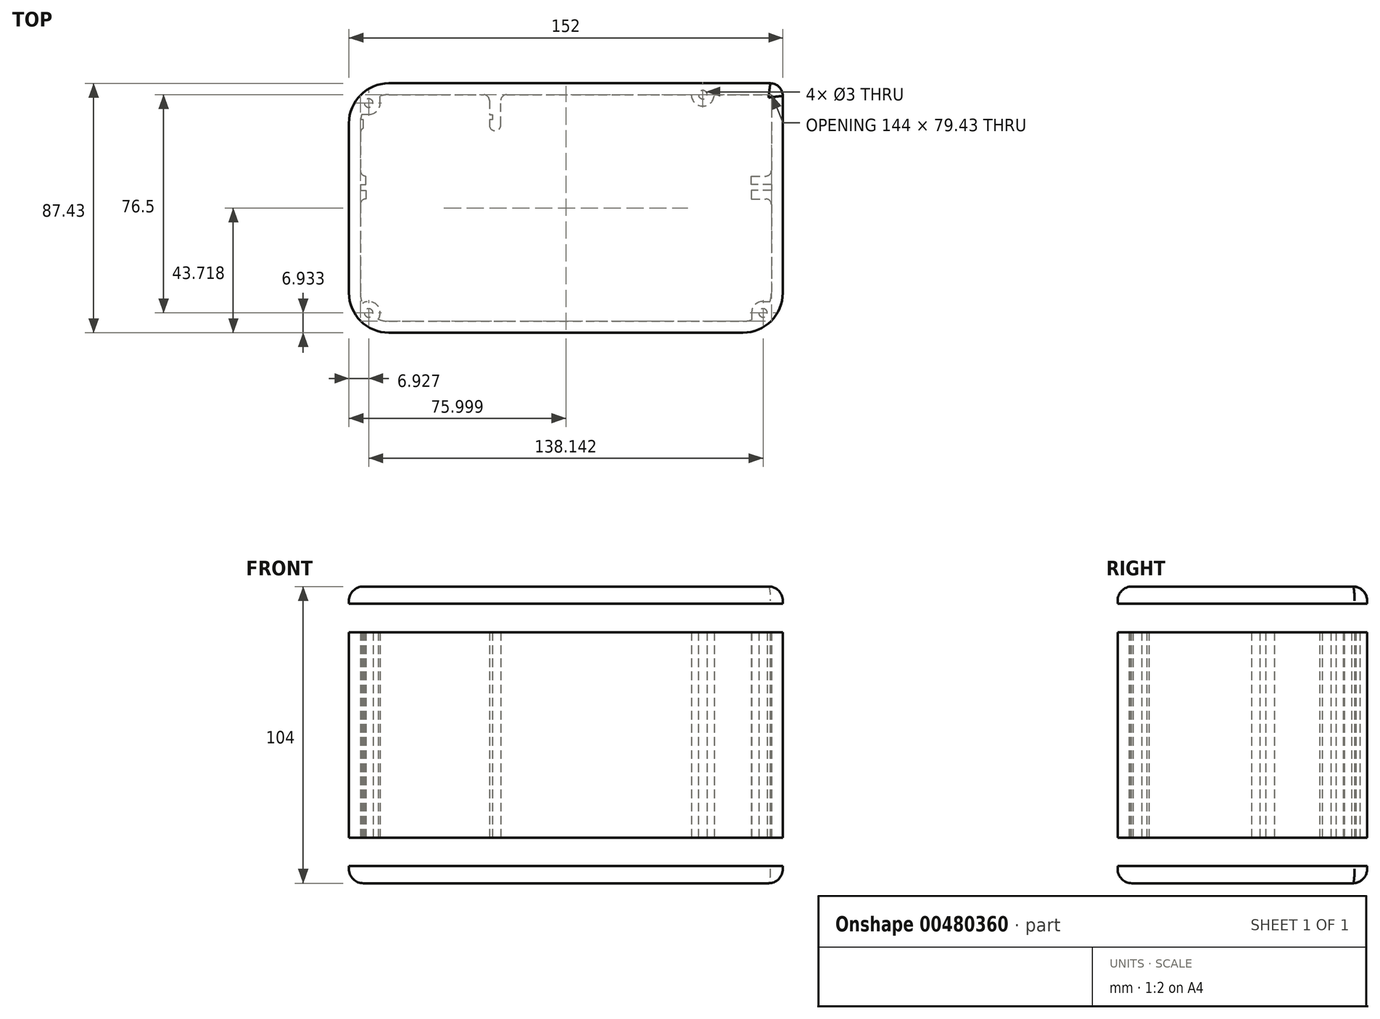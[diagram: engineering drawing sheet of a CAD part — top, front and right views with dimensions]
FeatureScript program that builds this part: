
annotation { "Feature Type Name" : "Feature", "Feature Type Description" : "" }
export const myFeature = defineFeature(function(context is Context, id is Id, definition is map)
    precondition{}
    {
        {
            var Q0;
            Q0=qCreatedBy(makeId("Top.planeOp"),FACE);
            var sketch = newSketch(context, id + "F0", { "sketchPlane" : qUnion([Q0])});
            skLineSegment(sketch, "E0.bottom", {"start": v(-110.78, -6.54) * mm, "end": v(28.22, -6.54) * mm, "construction": true});
            skLineSegment(sketch, "E0.top", {"start": v(-110.78, -8.34) * mm, "end": v(28.22, -8.34) * mm, "construction": true});
            skLineSegment(sketch, "E0.left", {"start": v(-110.78, -6.54) * mm, "end": v(-110.78, -8.34) * mm});
            skLineSegment(sketch, "E0.right", {"start": v(28.22, -6.54) * mm, "end": v(28.22, -8.34) * mm});
            skLineSegment(sketch, "E1.left", {"start": v(-107.28, -22.34) * mm, "end": v(-107.28, -42.34) * mm, "construction": true});
            skLineSegment(sketch, "E2.right", {"start": v(29.72, -22.34) * mm, "end": v(29.72, -42.34) * mm, "construction": true});
            skLineSegment(sketch, "E3.bottom", {"start": v(-100.78, 25.1) * mm, "end": v(32.82, 25.1) * mm});
            skLineSegment(sketch, "E3.top", {"start": v(-100.78, -54.34) * mm, "end": v(23.22, -54.34) * mm});
            skLineSegment(sketch, "E3.left", {"start": v(-110.78, 15.1) * mm, "end": v(-110.78, -44.34) * mm});
            skLineSegment(sketch, "E3.right", {"start": v(33.22, 24.7) * mm, "end": v(33.22, -44.34) * mm});
            skPoint(sketch, "E4", {"position": v(-38.78, -54.34) * mm});
            skPoint(sketch, "E5.visualSharp", {"position": v(-110.78, 25.1) * mm});
            skArc(sketch, "E5.filletArc", {"start": v(-100.78, 25.1) * mm, "mid": v(-107.85, 22.16) * mm, "end": v(-110.78, 15.1) * mm});
            skPoint(sketch, "E6.visualSharp", {"position": v(33.22, 25.1) * mm});
            skArc(sketch, "E6.filletArc", {"start": v(33.22, 24.7) * mm, "mid": v(33.1, 24.98) * mm, "end": v(32.82, 25.1) * mm});
            skPoint(sketch, "E7.visualSharp", {"position": v(33.22, -54.34) * mm});
            skArc(sketch, "E7.filletArc", {"start": v(23.22, -54.34) * mm, "mid": v(30.29, -51.4) * mm, "end": v(33.22, -44.34) * mm});
            skPoint(sketch, "E8.visualSharp", {"position": v(-110.78, -54.34) * mm});
            skArc(sketch, "E8.filletArc", {"start": v(-110.78, -44.34) * mm, "mid": v(-107.85, -51.4) * mm, "end": v(-100.78, -54.34) * mm});
            skLineSegment(sketch, "E9.0", {"start": v(-100.78, 29.1) * mm, "end": v(32.82, 29.1) * mm});
            skArc(sketch, "E9.1", {"start": v(37.22, 24.7) * mm, "mid": v(35.93, 27.8) * mm, "end": v(32.82, 29.1) * mm});
            skArc(sketch, "E9.2", {"start": v(-100.78, 29.1) * mm, "mid": v(-110.68, 25) * mm, "end": v(-114.78, 15.1) * mm});
            skLineSegment(sketch, "E9.3", {"start": v(37.22, 24.7) * mm, "end": v(37.22, -44.34) * mm});
            skLineSegment(sketch, "E9.4", {"start": v(-114.78, 15.1) * mm, "end": v(-114.78, -44.34) * mm});
            skArc(sketch, "E9.5", {"start": v(-114.78, -44.34) * mm, "mid": v(-110.68, -54.24) * mm, "end": v(-100.78, -58.34) * mm});
            skLineSegment(sketch, "E9.6", {"start": v(-100.78, -58.34) * mm, "end": v(23.22, -58.34) * mm});
            skArc(sketch, "E9.7", {"start": v(23.22, -58.34) * mm, "mid": v(33.12, -54.24) * mm, "end": v(37.22, -44.34) * mm});
            skLineSegment(sketch, "E10", {"start": v(-97.28, -12.34) * mm, "end": v(19.72, -12.34) * mm, "construction": true});
            skLineSegment(sketch, "E11", {"start": v(19.72, -52.34) * mm, "end": v(-97.28, -52.34) * mm, "construction": true});
            skLineSegment(sketch, "E12", {"start": v(-35.28, -12.34) * mm, "end": v(-35.28, -52.34) * mm, "construction": true});
            skPoint(sketch, "E13", {"position": v(-38.78, -12.34) * mm});
            skPoint(sketch, "E14.visualSharp", {"position": v(-107.28, -12.34) * mm});
            skArc(sketch, "E14.filletArc", {"start": v(-97.28, -12.34) * mm, "mid": v(-104.35, -15.27) * mm, "end": v(-107.28, -22.34) * mm, "construction": true});
            skPoint(sketch, "E15.visualSharp", {"position": v(-107.28, -52.34) * mm});
            skArc(sketch, "E15.filletArc", {"start": v(-107.28, -42.34) * mm, "mid": v(-104.35, -49.4) * mm, "end": v(-97.28, -52.34) * mm, "construction": true});
            skPoint(sketch, "E16.visualSharp", {"position": v(29.72, -52.34) * mm});
            skArc(sketch, "E16.filletArc", {"start": v(19.72, -52.34) * mm, "mid": v(26.79, -49.4) * mm, "end": v(29.72, -42.34) * mm, "construction": true});
            skPoint(sketch, "E17.visualSharp", {"position": v(29.72, -12.34) * mm});
            skArc(sketch, "E17.filletArc", {"start": v(29.72, -22.34) * mm, "mid": v(26.79, -15.27) * mm, "end": v(19.72, -12.34) * mm, "construction": true});
            skCircle(sketch, "E18", {"center": v(-107.85, 22.16) * mm, "radius": 4 * mm});
            skLineSegment(sketch, "E19", {"start": v(-100.78, 15.1) * mm, "end": v(-110.78, 25.1) * mm, "construction": true});
            skCircle(sketch, "E20", {"center": v(30.29, -51.4) * mm, "radius": 4 * mm});
            skLineSegment(sketch, "E21", {"start": v(23.22, -44.34) * mm, "end": v(33.22, -54.34) * mm, "construction": true});
            skCircle(sketch, "E22", {"center": v(-107.85, -51.4) * mm, "radius": 4 * mm});
            skLineSegment(sketch, "E23", {"start": v(-100.78, -44.34) * mm, "end": v(-110.78, -54.34) * mm, "construction": true});
            skLineSegment(sketch, "E24.bottom", {"start": v(-110.78, 18.06) * mm, "end": v(-64.58, 18.06) * mm});
            skLineSegment(sketch, "E24.top", {"start": v(-110.78, 16.46) * mm, "end": v(-64.58, 16.46) * mm});
            skLineSegment(sketch, "E24.left", {"start": v(-110.78, 18.06) * mm, "end": v(-110.78, 16.46) * mm});
            skLineSegment(sketch, "E24.right", {"start": v(-64.58, 18.06) * mm, "end": v(-64.58, 16.46) * mm});
            skLineSegment(sketch, "E25", {"start": v(-65.58, 25.1) * mm, "end": v(-65.58, 18.16) * mm});
            skLineSegment(sketch, "E26", {"start": v(-65.58, 18.16) * mm, "end": v(-64.58, 18.16) * mm});
            skLineSegment(sketch, "E27", {"start": v(-64.58, 18.16) * mm, "end": v(-64.58, 16.36) * mm});
            skLineSegment(sketch, "E28", {"start": v(-64.58, 16.36) * mm, "end": v(-65.58, 16.36) * mm});
            skLineSegment(sketch, "E29", {"start": v(-65.58, 16.36) * mm, "end": v(-65.58, 12.47) * mm});
            skLineSegment(sketch, "E30", {"start": v(-65.58, 12.47) * mm, "end": v(-61.58, 12.47) * mm});
            skLineSegment(sketch, "E31", {"start": v(-61.58, 12.47) * mm, "end": v(-61.58, 25.1) * mm});
            skPoint(sketch, "E32", {"position": v(-64.58, 17.26) * mm});
            skLineSegment(sketch, "E33", {"start": v(-110.78, 13.36) * mm, "end": v(-109.78, 13.36) * mm});
            skLineSegment(sketch, "E34", {"start": v(-109.78, 13.36) * mm, "end": v(-109.78, 16.36) * mm});
            skLineSegment(sketch, "E35", {"start": v(-109.78, 16.36) * mm, "end": v(-110.78, 16.36) * mm});
            skLineSegment(sketch, "E36", {"start": v(-107.85, 18.16) * mm, "end": v(-110.3, 18.16) * mm});
            skLineSegment(sketch, "E37", {"start": v(-103.85, 22.16) * mm, "end": v(-103.85, 24.6) * mm});
            skLineSegment(sketch, "E38", {"start": v(-107.85, -47.4) * mm, "end": v(-110.3, -47.4) * mm});
            skLineSegment(sketch, "E39", {"start": v(-103.85, -51.4) * mm, "end": v(-103.85, -53.85) * mm});
            skLineSegment(sketch, "E40", {"start": v(30.29, -47.4) * mm, "end": v(32.74, -47.4) * mm});
            skLineSegment(sketch, "E41", {"start": v(26.29, -51.4) * mm, "end": v(26.29, -53.85) * mm});
            skLineSegment(sketch, "E42", {"start": v(-110.78, -6.44) * mm, "end": v(-108.78, -6.44) * mm});
            skLineSegment(sketch, "E43", {"start": v(-108.78, -6.44) * mm, "end": v(-108.78, -3.44) * mm});
            skLineSegment(sketch, "E44", {"start": v(-108.78, -3.44) * mm, "end": v(-110.78, -3.44) * mm});
            skLineSegment(sketch, "E45", {"start": v(-110.78, -8.44) * mm, "end": v(-108.78, -8.44) * mm});
            skLineSegment(sketch, "E46", {"start": v(-108.78, -8.44) * mm, "end": v(-108.78, -11.44) * mm});
            skLineSegment(sketch, "E47", {"start": v(-108.78, -11.44) * mm, "end": v(-110.78, -11.44) * mm});
            skLineSegment(sketch, "E48", {"start": v(33.22, -6.44) * mm, "end": v(26.22, -6.44) * mm});
            skLineSegment(sketch, "E49", {"start": v(26.22, -6.44) * mm, "end": v(26.22, -3.44) * mm});
            skLineSegment(sketch, "E50", {"start": v(33.22, -8.44) * mm, "end": v(26.22, -8.44) * mm});
            skLineSegment(sketch, "E51", {"start": v(26.22, -8.44) * mm, "end": v(26.22, -11.44) * mm});
            skLineSegment(sketch, "E52", {"start": v(26.22, -11.44) * mm, "end": v(33.22, -11.44) * mm});
            skLineSegment(sketch, "E53", {"start": v(26.22, -3.44) * mm, "end": v(33.22, -3.44) * mm});
            skLineSegment(sketch, "E54", {"start": v(28.22, -6.44) * mm, "end": v(28.22, -8.44) * mm});
            skCircle(sketch, "E55", {"center": v(9.18, 25.1) * mm, "radius": 4 * mm});
            skCircle(sketch, "E56", {"center": v(9.18, 25.1) * mm, "radius": 1.5 * mm});
            skCircle(sketch, "E57", {"center": v(-107.85, 22.16) * mm, "radius": 1.5 * mm});
            skCircle(sketch, "E58", {"center": v(-107.85, -51.4) * mm, "radius": 1.5 * mm});
            skCircle(sketch, "E59", {"center": v(30.29, -51.4) * mm, "radius": 1.5 * mm});
            skSolve(sketch);
        }
        {
            var Q0;
            Q0=makeQuery(id+"F0.imprint","IMPRINT",FACE,{"disambiguationData":[TD([[makeQuery(id+"F0.imprint","IMPRINT",EDGE,{"derivedFrom":sQuery(id+"F0.wireOp",EDGE,"E3.bottom")}),1.0]])]});
            var Q1;
            {var subQ0=sQuery(id+"F0.wireOp",EDGE,"E18");var subQ1=sQuery(id+"F0.wireOp",EDGE,"E5.filletArc");var subQ2=makeQuery(id+"F0.imprint","INTERSECT",VERTEX,{"disambiguationData":[OD(0.0)],"derivedFrom":[subQ1,subQ0]});Q1=makeQuery(id+"F0.imprint","IMPRINT",FACE,{"disambiguationData":[TD([[makeQuery(id+"F0.imprint","IMPRINT",EDGE,{"disambiguationData":[TD([[subQ2,-1.0]])],"derivedFrom":subQ1}),-1.0]])]});}
            var Q2;
            {var subQ3=sQuery(id+"F0.wireOp",EDGE,"E25");Q2=makeQuery(id+"F0.imprint","IMPRINT",FACE,{"disambiguationData":[TD([[makeQuery(id+"F0.imprint","IMPRINT",EDGE,{"derivedFrom":subQ3}),1.0]])]});}
            var Q3;
            {var subQ1=sQuery(id+"F0.wireOp",EDGE,"E33");Q3=makeQuery(id+"F0.imprint","IMPRINT",FACE,{"disambiguationData":[TD([[makeQuery(id+"F0.imprint","IMPRINT",EDGE,{"derivedFrom":subQ1}),1.0]])]});}
            var Q4;
            {var subQ0=sQuery(id+"F0.wireOp",EDGE,"E37");Q4=makeQuery(id+"F0.imprint","IMPRINT",FACE,{"disambiguationData":[TD([[makeQuery(id+"F0.imprint","IMPRINT",EDGE,{"derivedFrom":subQ0}),1.0]])]});}
            var Q5;
            {var subQ0=sQuery(id+"F0.wireOp",EDGE,"E18");var subQ1=sQuery(id+"F0.wireOp",EDGE,"E5.filletArc");var subQ2=makeQuery(id+"F0.imprint","INTERSECT",VERTEX,{"disambiguationData":[OD(0.0)],"derivedFrom":[subQ1,subQ0]});Q5=makeQuery(id+"F0.imprint","IMPRINT",FACE,{"disambiguationData":[TD([[makeQuery(id+"F0.imprint","IMPRINT",EDGE,{"disambiguationData":[TD([[subQ2,-1.0]])],"derivedFrom":subQ1}),1.0]])]});}
            var Q6;
            {var subQ0=sQuery(id+"F0.wireOp",EDGE,"E36");Q6=makeQuery(id+"F0.imprint","IMPRINT",FACE,{"disambiguationData":[TD([[makeQuery(id+"F0.imprint","IMPRINT",EDGE,{"derivedFrom":subQ0}),-1.0]])]});}
            var Q7;
            {var subQ0=sQuery(id+"F0.wireOp",EDGE,"98a416b9-4927-4f26-95ba-e2e42b6dbb6d");var subQ1=sQuery(id+"F0.wireOp",EDGE,"E6.filletArc");var subQ2=makeQuery(id+"F0.imprint","INTERSECT",VERTEX,{"disambiguationData":[OD(0.0)],"derivedFrom":[subQ1,subQ0]});Q7=makeQuery(id+"F0.imprint","IMPRINT",FACE,{"disambiguationData":[TD([[makeQuery(id+"F0.imprint","IMPRINT",EDGE,{"disambiguationData":[TD([[subQ2,-1.0]])],"derivedFrom":subQ1}),-1.0]])]});}
            var Q8;
            {var subQ0=sQuery(id+"F0.wireOp",EDGE,"7a0X1hN1-dMAj-nVcP-FXcl-xYdpotMuzt6M");Q8=makeQuery(id+"F0.imprint","IMPRINT",FACE,{"disambiguationData":[TD([[makeQuery(id+"F0.imprint","IMPRINT",EDGE,{"derivedFrom":subQ0}),-1.0]])]});}
            var Q9;
            {var subQ0=sQuery(id+"F0.wireOp",EDGE,"7hl1VtTn-0XGv-oFa7-S9O5-PqMMbb4nXPVR");Q9=makeQuery(id+"F0.imprint","IMPRINT",FACE,{"disambiguationData":[TD([[makeQuery(id+"F0.imprint","IMPRINT",EDGE,{"derivedFrom":subQ0}),1.0]])]});}
            var Q10;
            {var subQ1=sQuery(id+"F0.wireOp",EDGE,"E9.3");Q10=makeQuery(id+"F0.imprint","IMPRINT",FACE,{"disambiguationData":[TD([[makeQuery(id+"F0.imprint","IMPRINT",EDGE,{"derivedFrom":subQ1}),-1.0]])]});}
            var Q11;
            {var subQ0=sQuery(id+"F0.wireOp",EDGE,"E20");var subQ1=sQuery(id+"F0.wireOp",EDGE,"E7.filletArc");var subQ2=makeQuery(id+"F0.imprint","INTERSECT",VERTEX,{"disambiguationData":[OD(0.0)],"derivedFrom":[subQ1,subQ0]});Q11=makeQuery(id+"F0.imprint","IMPRINT",FACE,{"disambiguationData":[TD([[makeQuery(id+"F0.imprint","IMPRINT",EDGE,{"disambiguationData":[TD([[subQ2,-1.0]])],"derivedFrom":subQ1}),-1.0]])]});}
            var Q12;
            {var subQ0=sQuery(id+"F0.wireOp",EDGE,"E20");var subQ1=sQuery(id+"F0.wireOp",EDGE,"E7.filletArc");var subQ2=makeQuery(id+"F0.imprint","INTERSECT",VERTEX,{"disambiguationData":[OD(0.0)],"derivedFrom":[subQ1,subQ0]});Q12=makeQuery(id+"F0.imprint","IMPRINT",FACE,{"disambiguationData":[TD([[makeQuery(id+"F0.imprint","IMPRINT",EDGE,{"disambiguationData":[TD([[subQ2,-1.0]])],"derivedFrom":subQ1}),1.0]])]});}
            var Q13;
            {var subQ0=sQuery(id+"F0.wireOp",EDGE,"E40");var subQ1=sQuery(id+"F0.wireOp",EDGE,"E7.filletArc");var subQ2=makeQuery(id+"F0.imprint","INTERSECT",VERTEX,{"derivedFrom":[subQ1,subQ0]});Q13=makeQuery(id+"F0.imprint","IMPRINT",FACE,{"disambiguationData":[TD([[makeQuery(id+"F0.imprint","IMPRINT",EDGE,{"disambiguationData":[TD([[subQ2,1.0]])],"derivedFrom":subQ1}),1.0]])]});}
            var Q14;
            {var subQ0=sQuery(id+"F0.wireOp",EDGE,"E20");var subQ1=sQuery(id+"F0.wireOp",EDGE,"E16.filletArc");var subQ2=makeQuery(id+"F0.imprint","INTERSECT",VERTEX,{"disambiguationData":[OD(0.0)],"derivedFrom":[subQ1,subQ0]});Q14=makeQuery(id+"F0.imprint","IMPRINT",FACE,{"disambiguationData":[TD([[makeQuery(id+"F0.imprint","IMPRINT",EDGE,{"disambiguationData":[TD([[subQ2,-1.0]])],"derivedFrom":subQ1}),1.0]])]});}
            var Q15;
            {var subQ0=sQuery(id+"F0.wireOp",EDGE,"E41");var subQ1=sQuery(id+"F0.wireOp",EDGE,"E7.filletArc");var subQ2=makeQuery(id+"F0.imprint","INTERSECT",VERTEX,{"derivedFrom":[subQ1,subQ0]});Q15=makeQuery(id+"F0.imprint","IMPRINT",FACE,{"disambiguationData":[TD([[makeQuery(id+"F0.imprint","IMPRINT",EDGE,{"disambiguationData":[TD([[subQ2,-1.0]])],"derivedFrom":subQ1}),1.0]])]});}
            var Q16;
            {var subQ9=sQuery(id+"F0.wireOp",EDGE,"E3.top");Q16=makeQuery(id+"F0.imprint","IMPRINT",FACE,{"disambiguationData":[TD([[makeQuery(id+"F0.imprint","IMPRINT",EDGE,{"derivedFrom":subQ9}),-1.0]])]});}
            var Q17;
            {var subQ0=sQuery(id+"F0.wireOp",EDGE,"E22");var subQ1=sQuery(id+"F0.wireOp",EDGE,"E8.filletArc");var subQ2=makeQuery(id+"F0.imprint","INTERSECT",VERTEX,{"disambiguationData":[OD(0.0)],"derivedFrom":[subQ1,subQ0]});Q17=makeQuery(id+"F0.imprint","IMPRINT",FACE,{"disambiguationData":[TD([[makeQuery(id+"F0.imprint","IMPRINT",EDGE,{"disambiguationData":[TD([[subQ2,-1.0]])],"derivedFrom":subQ1}),-1.0]])]});}
            var Q18;
            {var subQ0=sQuery(id+"F0.wireOp",EDGE,"E22");var subQ1=sQuery(id+"F0.wireOp",EDGE,"E8.filletArc");var subQ2=makeQuery(id+"F0.imprint","INTERSECT",VERTEX,{"disambiguationData":[OD(0.0)],"derivedFrom":[subQ1,subQ0]});Q18=makeQuery(id+"F0.imprint","IMPRINT",FACE,{"disambiguationData":[TD([[makeQuery(id+"F0.imprint","IMPRINT",EDGE,{"disambiguationData":[TD([[subQ2,-1.0]])],"derivedFrom":subQ1}),1.0]])]});}
            var Q19;
            {var subQ0=sQuery(id+"F0.wireOp",EDGE,"E22");var subQ1=sQuery(id+"F0.wireOp",EDGE,"E15.filletArc");var subQ2=makeQuery(id+"F0.imprint","INTERSECT",VERTEX,{"disambiguationData":[OD(0.0)],"derivedFrom":[subQ1,subQ0]});Q19=makeQuery(id+"F0.imprint","IMPRINT",FACE,{"disambiguationData":[TD([[makeQuery(id+"F0.imprint","IMPRINT",EDGE,{"disambiguationData":[TD([[subQ2,-1.0]])],"derivedFrom":subQ1}),1.0]])]});}
            var Q20;
            {var subQ0=sQuery(id+"F0.wireOp",EDGE,"E48");Q20=makeQuery(id+"F0.imprint","IMPRINT",FACE,{"disambiguationData":[TD([[makeQuery(id+"F0.imprint","IMPRINT",EDGE,{"derivedFrom":subQ0}),-1.0]])]});}
            var Q21;
            {var subQ0=sQuery(id+"F0.wireOp",EDGE,"E50");Q21=makeQuery(id+"F0.imprint","IMPRINT",FACE,{"disambiguationData":[TD([[makeQuery(id+"F0.imprint","IMPRINT",EDGE,{"derivedFrom":subQ0}),1.0]])]});}
            var Q22;
            {var subQ0=sQuery(id+"F0.wireOp",EDGE,"E42");Q22=makeQuery(id+"F0.imprint","IMPRINT",FACE,{"disambiguationData":[TD([[makeQuery(id+"F0.imprint","IMPRINT",EDGE,{"derivedFrom":subQ0}),1.0]])]});}
            var Q23;
            {var subQ0=sQuery(id+"F0.wireOp",EDGE,"E45");Q23=makeQuery(id+"F0.imprint","IMPRINT",FACE,{"disambiguationData":[TD([[makeQuery(id+"F0.imprint","IMPRINT",EDGE,{"derivedFrom":subQ0}),-1.0]])]});}
            var Q24;
            {var subQ0=sQuery(id+"F0.wireOp",EDGE,"E54");var subQ3=makeQuery(id+"F0.imprint","IMPRINT",VERTEX,{"disambiguationData":[OD(0.0)],"derivedFrom":subQ0});Q24=makeQuery(id+"F0.imprint","IMPRINT",FACE,{"disambiguationData":[TD([[makeQuery(id+"F0.imprint","IMPRINT",EDGE,{"disambiguationData":[TD([[subQ3,-1.0]])],"derivedFrom":subQ0}),1.0]])]});}
            var Q25;
            {var subQ0=sQuery(id+"F0.wireOp",EDGE,"E55");var subQ1=sQuery(id+"F0.wireOp",EDGE,"E3.bottom");var subQ2=makeQuery(id+"F0.imprint","INTERSECT",VERTEX,{"disambiguationData":[OD(0.0)],"derivedFrom":[subQ1,subQ0]});Q25=makeQuery(id+"F0.imprint","IMPRINT",FACE,{"disambiguationData":[TD([[makeQuery(id+"F0.imprint","IMPRINT",EDGE,{"disambiguationData":[TD([[subQ2,-1.0]])],"derivedFrom":subQ1}),1.0]])]});}
            var Q26;
            {var subQ0=sQuery(id+"F0.wireOp",EDGE,"E55");var subQ1=sQuery(id+"F0.wireOp",EDGE,"E3.bottom");var subQ2=makeQuery(id+"F0.imprint","INTERSECT",VERTEX,{"disambiguationData":[OD(0.0)],"derivedFrom":[subQ1,subQ0]});Q26=makeQuery(id+"F0.imprint","IMPRINT",FACE,{"disambiguationData":[TD([[makeQuery(id+"F0.imprint","IMPRINT",EDGE,{"disambiguationData":[TD([[subQ2,-1.0]])],"derivedFrom":subQ1}),-1.0]])]});}
            var Q27;
            {var subQ4=sQuery(id+"F0.wireOp",EDGE,"E9.4");Q27=makeQuery(id+"F0.imprint","IMPRINT",FACE,{"disambiguationData":[TD([[makeQuery(id+"F0.imprint","IMPRINT",EDGE,{"derivedFrom":subQ4}),1.0]])]});}
            var Q28;
            {var subQ5=sQuery(id+"F0.wireOp",EDGE,"E24.left");Q28=makeQuery(id+"F0.imprint","IMPRINT",FACE,{"disambiguationData":[TD([[makeQuery(id+"F0.imprint","IMPRINT",EDGE,{"derivedFrom":subQ5}),1.0]])]});}
            extrude(context, id + "F1", {"entities" : qUnion([Q0, Q1, Q2, Q3, Q4, Q5, Q6, Q7, Q8, Q9, Q10, Q11, Q12, Q13, Q14, Q15, Q16, Q17, Q18, Q19, Q20, Q21, Q22, Q23, Q24, Q25, Q26, Q27, Q28]), "depth" : 72 * mm, "offsetDistance" : 25 * mm});
        }
        {
            var Q0;
            Q0=makeQuery(id+"F1.opExtrude","CAP_FACE",FACE,{"disambiguationData":[OSD([sQuery(id+"F0.wireOp",EDGE,"ac47ddaa-1ff9-4fb7-91e3-0095d18774f8.0"),sQuery(id+"F0.wireOp",EDGE,"ac47ddaa-1ff9-4fb7-91e3-0095d18774f8.1"),sQuery(id+"F0.wireOp",EDGE,"ac47ddaa-1ff9-4fb7-91e3-0095d18774f8.2"),sQuery(id+"F0.wireOp",EDGE,"23e3ad9c-f10d-46c0-9b1d-762057cb4504"),sQuery(id+"F0.wireOp",EDGE,"20860ca5-1e23-45d1-b3d5-98853785f5a3.filletArc"),sQuery(id+"F0.wireOp",EDGE,"e5807837-fe32-4673-91be-abad1df8b40d.filletArc"),sQuery(id+"F0.wireOp",EDGE,"52051394-9daf-43b8-8cdd-08482cc01996.filletArc"),sQuery(id+"F0.wireOp",EDGE,"ed5e0c1f-c6d5-438c-b0a1-3757e7beccb2.filletArc"),sQuery(id+"F0.wireOp",EDGE,"8e21b9bb-f049-4d82-9402-97ffcd915d1b.0"),sQuery(id+"F0.wireOp",EDGE,"8e21b9bb-f049-4d82-9402-97ffcd915d1b.1"),sQuery(id+"F0.wireOp",EDGE,"8e21b9bb-f049-4d82-9402-97ffcd915d1b.2"),sQuery(id+"F0.wireOp",EDGE,"8e21b9bb-f049-4d82-9402-97ffcd915d1b.3"),sQuery(id+"F0.wireOp",EDGE,"8e21b9bb-f049-4d82-9402-97ffcd915d1b.4"),sQuery(id+"F0.wireOp",EDGE,"8e21b9bb-f049-4d82-9402-97ffcd915d1b.5"),sQuery(id+"F0.wireOp",EDGE,"8e21b9bb-f049-4d82-9402-97ffcd915d1b.6"),sQuery(id+"F0.wireOp",EDGE,"8e21b9bb-f049-4d82-9402-97ffcd915d1b.7")])],"isStart":false});
            var Q1;
            Q1=makeQuery(id+"F1.opExtrude","CAP_FACE",FACE,{"disambiguationData":[OSD([sQuery(id+"F0.wireOp",EDGE,"E3.bottom"),sQuery(id+"F0.wireOp",EDGE,"E3.top"),sQuery(id+"F0.wireOp",EDGE,"E3.left"),sQuery(id+"F0.wireOp",EDGE,"E3.right"),sQuery(id+"F0.wireOp",EDGE,"e5adbce5-5c82-4fed-9f0c-1d366584b07e.0"),sQuery(id+"F0.wireOp",EDGE,"e5adbce5-5c82-4fed-9f0c-1d366584b07e.1"),sQuery(id+"F0.wireOp",EDGE,"e5adbce5-5c82-4fed-9f0c-1d366584b07e.2"),sQuery(id+"F0.wireOp",EDGE,"e5adbce5-5c82-4fed-9f0c-1d366584b07e.3")])],"isStart":false});
            cPlane(context, id + "F2", {"entities" : qUnion([Q0, Q1]), "cplaneType" : CPlaneType.OFFSET, "offset" : 10 * mm, "width" : 150 * mm, "height" : 150 * mm});
        }
        {
            var Q0;
            Q0=qCreatedBy(id+"F2.planeOp",FACE);
            var sketch = newSketch(context, id + "F3", { "sketchPlane" : qUnion([Q0])});
            skLineSegment(sketch, "E60.0", {"start": v(-100.78, 29.1) * mm, "end": v(32.82, 29.1) * mm});
            skArc(sketch, "E60.1", {"start": v(-100.78, 29.1) * mm, "mid": v(-110.68, 25) * mm, "end": v(-114.78, 15.1) * mm});
            skLineSegment(sketch, "E60.2", {"start": v(-114.78, 15.1) * mm, "end": v(-114.78, -44.34) * mm});
            skArc(sketch, "E60.3", {"start": v(-114.78, -44.34) * mm, "mid": v(-110.68, -54.24) * mm, "end": v(-100.78, -58.34) * mm});
            skLineSegment(sketch, "E60.4", {"start": v(-100.78, -58.34) * mm, "end": v(23.22, -58.34) * mm});
            skArc(sketch, "E60.5", {"start": v(23.22, -58.34) * mm, "mid": v(33.12, -54.24) * mm, "end": v(37.22, -44.34) * mm});
            skLineSegment(sketch, "E60.6", {"start": v(37.22, 24.7) * mm, "end": v(37.22, -44.34) * mm});
            skArc(sketch, "E60.7", {"start": v(37.22, 24.7) * mm, "mid": v(35.93, 27.8) * mm, "end": v(32.82, 29.1) * mm});
            skSolve(sketch);
        }
        {
            var Q0;
            Q0=makeQuery(id+"F1.opExtrude","CAP_FACE",FACE,{"disambiguationData":[OSD([sQuery(id+"F0.wireOp",EDGE,"ac47ddaa-1ff9-4fb7-91e3-0095d18774f8.0"),sQuery(id+"F0.wireOp",EDGE,"ac47ddaa-1ff9-4fb7-91e3-0095d18774f8.1"),sQuery(id+"F0.wireOp",EDGE,"ac47ddaa-1ff9-4fb7-91e3-0095d18774f8.2"),sQuery(id+"F0.wireOp",EDGE,"23e3ad9c-f10d-46c0-9b1d-762057cb4504"),sQuery(id+"F0.wireOp",EDGE,"20860ca5-1e23-45d1-b3d5-98853785f5a3.filletArc"),sQuery(id+"F0.wireOp",EDGE,"e5807837-fe32-4673-91be-abad1df8b40d.filletArc"),sQuery(id+"F0.wireOp",EDGE,"52051394-9daf-43b8-8cdd-08482cc01996.filletArc"),sQuery(id+"F0.wireOp",EDGE,"ed5e0c1f-c6d5-438c-b0a1-3757e7beccb2.filletArc"),sQuery(id+"F0.wireOp",EDGE,"8e21b9bb-f049-4d82-9402-97ffcd915d1b.0"),sQuery(id+"F0.wireOp",EDGE,"8e21b9bb-f049-4d82-9402-97ffcd915d1b.1"),sQuery(id+"F0.wireOp",EDGE,"8e21b9bb-f049-4d82-9402-97ffcd915d1b.2"),sQuery(id+"F0.wireOp",EDGE,"8e21b9bb-f049-4d82-9402-97ffcd915d1b.3"),sQuery(id+"F0.wireOp",EDGE,"8e21b9bb-f049-4d82-9402-97ffcd915d1b.4"),sQuery(id+"F0.wireOp",EDGE,"8e21b9bb-f049-4d82-9402-97ffcd915d1b.5"),sQuery(id+"F0.wireOp",EDGE,"8e21b9bb-f049-4d82-9402-97ffcd915d1b.6"),sQuery(id+"F0.wireOp",EDGE,"8e21b9bb-f049-4d82-9402-97ffcd915d1b.7")])],"isStart":true});
            var Q1;
            Q1=makeQuery(id+"F0.imprint","IMPRINT",FACE,{"disambiguationData":[TD([[makeQuery(id+"F0.imprint","IMPRINT",EDGE,{"derivedFrom":sQuery(id+"F0.wireOp",EDGE,"E3.bottom")}),1.0]])]});
            cPlane(context, id + "F4", {"entities" : qUnion([Q0, Q1]), "cplaneType" : CPlaneType.OFFSET, "offset" : 10 * mm, "oppositeDirection" : true, "width" : 150 * mm, "height" : 150 * mm});
        }
        {
            var Q0;
            Q0=qCreatedBy(id+"F4.planeOp",FACE);
            var sketch = newSketch(context, id + "F5", { "sketchPlane" : qUnion([Q0])});
            skArc(sketch, "E61.0", {"start": v(-114.78, -44.34) * mm, "mid": v(-110.68, -54.24) * mm, "end": v(-100.78, -58.34) * mm});
            skLineSegment(sketch, "E61.1", {"start": v(-100.78, -58.34) * mm, "end": v(23.22, -58.34) * mm});
            skArc(sketch, "E61.2", {"start": v(23.22, -58.34) * mm, "mid": v(33.12, -54.24) * mm, "end": v(37.22, -44.34) * mm});
            skLineSegment(sketch, "E61.3", {"start": v(37.22, 24.7) * mm, "end": v(37.22, -44.34) * mm});
            skArc(sketch, "E61.4", {"start": v(37.22, 24.7) * mm, "mid": v(35.93, 27.8) * mm, "end": v(32.82, 29.1) * mm});
            skLineSegment(sketch, "E61.5", {"start": v(-100.78, 29.1) * mm, "end": v(32.82, 29.1) * mm});
            skArc(sketch, "E61.6", {"start": v(-100.78, 29.1) * mm, "mid": v(-110.68, 25) * mm, "end": v(-114.78, 15.1) * mm});
            skLineSegment(sketch, "E61.7", {"start": v(-114.78, 15.1) * mm, "end": v(-114.78, -44.34) * mm});
            skSolve(sketch);
        }
        {
            var Q0;
            Q0=qSketchRegion(id+"F5",true);
            extrude(context, id + "F6", {"entities" : qUnion([Q0]), "oppositeDirection" : true, "depth" : 6 * mm});
        }
        {
            var Q0;
            Q0=qSketchRegion(id+"F3",true);
            extrude(context, id + "F7", {"entities" : qUnion([Q0]), "depth" : 6 * mm});
        }
        {
            var Q0;
            Q0=makeQuery(id+"F7.opExtrude","CAP_FACE",FACE,{"disambiguationData":[OSD([sQuery(id+"F3.wireOp",EDGE,"E60.0"),sQuery(id+"F3.wireOp",EDGE,"E60.1"),sQuery(id+"F3.wireOp",EDGE,"E60.2"),sQuery(id+"F3.wireOp",EDGE,"E60.3"),sQuery(id+"F3.wireOp",EDGE,"E60.4"),sQuery(id+"F3.wireOp",EDGE,"E60.5"),sQuery(id+"F3.wireOp",EDGE,"E60.6"),sQuery(id+"F3.wireOp",EDGE,"E60.7")])],"isStart":false});
            var Q1;
            Q1=makeQuery(id+"F6.opExtrude","CAP_FACE",FACE,{"disambiguationData":[OSD([sQuery(id+"F5.wireOp",EDGE,"E61.0"),sQuery(id+"F5.wireOp",EDGE,"E61.1"),sQuery(id+"F5.wireOp",EDGE,"E61.2"),sQuery(id+"F5.wireOp",EDGE,"E61.3"),sQuery(id+"F5.wireOp",EDGE,"E61.4"),sQuery(id+"F5.wireOp",EDGE,"E61.5"),sQuery(id+"F5.wireOp",EDGE,"E61.6"),sQuery(id+"F5.wireOp",EDGE,"E61.7")])],"isStart":false});
            fillet(context, id + "F8", {"entities" : qUnion([Q0, Q1]), "radius" : 5 * mm, "tangentPropagation" : true, "allowEdgeOverflow" : false});
        }
        {
            var Q0;
            Q0=makeQuery(id+"F1.opExtrude","SWEPT_EDGE",EDGE,{"disambiguationData":[OSD([sQuery(id+"F0.wireOp",EDGE,"E3.right"),sQuery(id+"F0.wireOp",EDGE,"E52")])]});
            var Q1;
            Q1=makeQuery(id+"F1.opExtrude","SWEPT_EDGE",EDGE,{"disambiguationData":[OSD([sQuery(id+"F0.wireOp",EDGE,"E3.right"),sQuery(id+"F0.wireOp",EDGE,"E53")])]});
            var Q2;
            Q2=makeQuery(id+"F1.opExtrude","SWEPT_EDGE",EDGE,{"disambiguationData":[OSD([sQuery(id+"F0.wireOp",EDGE,"E3.left"),sQuery(id+"F0.wireOp",EDGE,"E44")])]});
            var Q3;
            Q3=makeQuery(id+"F1.opExtrude","SWEPT_EDGE",EDGE,{"disambiguationData":[OSD([sQuery(id+"F0.wireOp",EDGE,"E3.left"),sQuery(id+"F0.wireOp",EDGE,"E47")])]});
            var Q4;
            Q4=makeQuery(id+"F1.opExtrude","SWEPT_EDGE",EDGE,{"disambiguationData":[OSD([sQuery(id+"F0.wireOp",EDGE,"E3.left"),sQuery(id+"F0.wireOp",EDGE,"E33")])]});
            var Q5;
            Q5=makeQuery(id+"F1.opExtrude","SWEPT_EDGE",EDGE,{"disambiguationData":[OSD([sQuery(id+"F0.wireOp",EDGE,"E3.bottom"),sQuery(id+"F0.wireOp",EDGE,"E31")])]});
            var Q6;
            Q6=makeQuery(id+"F1.opExtrude","SWEPT_EDGE",EDGE,{"disambiguationData":[OSD([sQuery(id+"F0.wireOp",EDGE,"E3.bottom"),sQuery(id+"F0.wireOp",EDGE,"E25")])]});
            var Q7;
            Q7=makeQuery(id+"F1.opExtrude","SWEPT_EDGE",EDGE,{"disambiguationData":[OSD([sQuery(id+"F0.wireOp",EDGE,"E29"),sQuery(id+"F0.wireOp",EDGE,"E30")])]});
            var Q8;
            Q8=makeQuery(id+"F1.opExtrude","SWEPT_EDGE",EDGE,{"disambiguationData":[OSD([sQuery(id+"F0.wireOp",EDGE,"E30"),sQuery(id+"F0.wireOp",EDGE,"E31")])]});
            fillet(context, id + "F9", {"entities" : qUnion([Q0, Q1, Q2, Q3, Q4, Q5, Q6, Q7, Q8]), "radius" : 2 * mm, "tangentPropagation" : true, "allowEdgeOverflow" : false});
        }
    });
